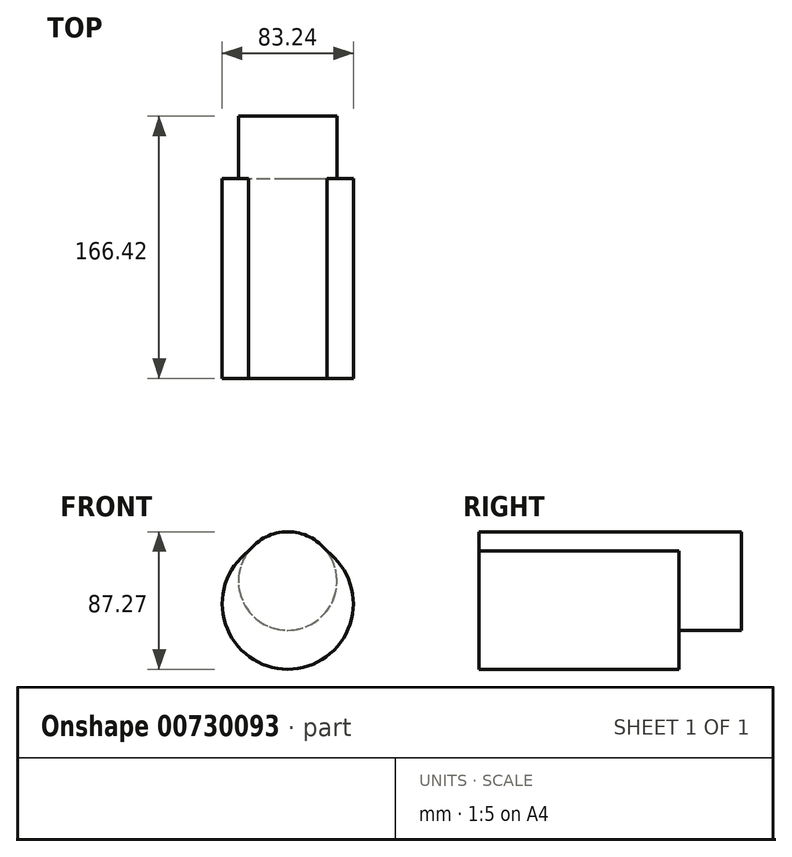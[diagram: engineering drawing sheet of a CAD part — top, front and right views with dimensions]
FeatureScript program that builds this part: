
annotation { "Feature Type Name" : "Feature", "Feature Type Description" : "" }
export const myFeature = defineFeature(function(context is Context, id is Id, definition is map)
    precondition{}
    {
        {
            var Q0;
            Q0=qCreatedBy(makeId("Front.planeOp"),FACE);
            var sketch = newSketch(context, id + "F0", { "sketchPlane" : qUnion([Q0])});
            skCircle(sketch, "E0", {"center": v(0, 0) * mm, "radius": 41.62 * mm});
            skSolve(sketch);
        }
        {
            var Q0;
            Q0 = qSketchRegion(id + "F0", true);
            extrude(context, id + "F1", {"entities" : qUnion([Q0]), "depth" : 127 * mm, "offsetDistance" : 25.4 * mm});
        }
        {
            var Q0;
            Q0=makeQuery(id+"F1.opExtrude","CAP_FACE",FACE,{"disambiguationData":[OSD([sQuery(id+"F0.wireOp",EDGE,"E0")])],"isStart":false});
            var sketch = newSketch(context, id + "F2", { "sketchPlane" : qUnion([Q0])});
            skLineSegment(sketch, "E1.bottom", {"start": v(0, 0) * mm, "end": v(0, 0) * mm});
            skLineSegment(sketch, "E1.top", {"start": v(0, 0) * mm, "end": v(0, 0) * mm});
            skLineSegment(sketch, "E1.left", {"start": v(0, 0) * mm, "end": v(0, 0) * mm});
            skLineSegment(sketch, "E1.right", {"start": v(0, 0) * mm, "end": v(0, 0) * mm});
            skCircle(sketch, "E2", {"center": v(0, 14.39) * mm, "radius": 31.26 * mm});
            skSolve(sketch);
        }
        {
            var Q0;
            Q0 = qSketchRegion(id + "F2", true);
            extrude(context, id + "F3", {"entities" : qUnion([Q0]), "operationType" : NewBodyOperationType.ADD, "oppositeDirection" : true, "depth" : 166.42 * mm, "offsetDistance" : 25.4 * mm});
        }
    });
